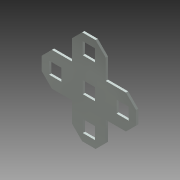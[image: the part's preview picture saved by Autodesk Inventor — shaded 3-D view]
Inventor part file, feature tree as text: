
AUTODESK INVENTOR PART (.ipt)
format: ipt  version: 2013 (Build 170138000, 138)  size: 175,104 bytes
history: native  units: mm (DEFAULTED — no unit token found)
features: extrude x6, other x5, sketch x3, pattern_linear x2
ambient origin geometry x8: Origin, YZ Plane, XZ Plane, XY Plane, X Axis, Y Axis, Z Axis, Center Point
bodies: Solid1 (feature_tree)
feature tree (16):
  extrude  "Extrusion1"  Depth=35.56mm
  pattern_linear  "Rectangular Pattern1"  Spacing1=12.7mm  [1 undecoded]
  pattern_linear  "Rectangular Pattern2"  Spacing1=12.7mm  [1 undecoded]
  sketch  "Sketch1"  dims[d0=35.56mm d1=35.56mm]
  sketch  "Sketch2"  dims[d2=12.7mm]
  other  "Srf1"
  other  "Srf2"
  other  "Srf3"
  sketch  "Sketch3"  dims[d3=12.7mm d4=12.7mm d5=12.7mm d6=11.43mm d7=11.43mm d8=11.43mm d9=11.43mm d10=3.81mm d11=3.81mm d12=3.81mm d13=3.81mm d14=3.81mm d15=3.81mm d16=3.81mm d17=3.81mm d18=3.81mm d19=3.81mm d20=3.81mm d21=3.81mm d22=3.81mm d23=3.81mm d24=3.81mm d25=3.81mm d26=4.572mm d27=4.572mm d28=4.572mm d29=4.572mm d30=4.572mm d31=4.572mm d32=4.572mm d33=4.572mm d34=4.572mm d35=4.572mm d36=2.794mm d37=2.794mm d38=2.794mm d39=2.794mm d40=4.064mm d41=4.064mm d42=11.43mm d43=0.8382mm d44=0.0mm d45=25.4mm d46=0.0mm d47=30.0mm d49=12.7mm d50=25.4mm d51=0.0mm d52=20.0mm d54=25.4mm d55=0.0mm d56=0.0mm d57=0.0mm d58=0.0mm d59=0.0mm d60=0.0mm d61=0.0mm d62=0.0mm d63=0.0mm d64=0.0mm]
  other  "Srf4"
  other  "Srf5"
  extrude  "ExtrusionSrf1"  Depth=11.43mm
  extrude  "ExtrusionSrf4"  Depth=11.43mm
  extrude  "ExtrusionSrf2"  Depth=11.43mm
  extrude  "ExtrusionSrf3"  Depth=11.43mm
  extrude  "ExtrusionSrf5"  Depth=3.81mm
note: 2 required parameter values undecoded (feature->parameter linkage not recoverable at this tier; creation-order binding heuristic only, values carry confidence <= 0.55)
